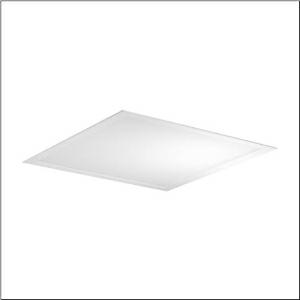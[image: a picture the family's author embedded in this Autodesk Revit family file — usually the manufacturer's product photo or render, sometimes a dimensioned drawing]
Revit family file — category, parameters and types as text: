
# Revit family: apollon_21_square_51mq11wc2454
name_source: partatom
category: Lighting Fixtures
units: mm (PartAtom-declared; Revit-internal decimal feet)

## family parameters
Cut with Voids When Loaded = No
Host = Face
Light Source = No
Part Type = Normal
Room Calculation Point = No
Round Connector Dimension = Use Diameter
Shared = No

## types (1)
- Apollon 21 square (1 x LED, 4200 lm, 24.7 W, 4000K)
    Apparent Load = 25 VA
    CIE Flux Codes = 60 87 97 100 100
    Color Rendering = 80
    Color Temperature = 4000K
    Default Elevation = 1800 mm
    Description = Apollon 21 square, office luminaire, primary optical cover: micro prismatic cover, of PMMA, CAT 2 (L<= 3000cd/m²), light emission: direct distribution, primary light characteristic: symmetric, installation type: lay-in mounting, LED, rated luminous flux: 4.200lm, luminous efficacy: 170lm/W, light colour: 840, colour temperature: 4000K, control gear: DALI 2, Multilumen, with terminal, 5-pole, mains connection: 220..240V, AC/DC, 0/50..60Hz, rated input power: 24.7W, housing, of aluminium, coated, traffic white (RAL 9016), module: M625, length: 620mm, width: 620mm, height: 55mm, recess depth: 180mm, housing upper side, of sheet steel, galvanised, protection rating (complete): IP20, protection rating (lamp compartment, on room side): IP54, insulation class (complete): insulation class II (safety insulation), certification: CE, ENEC, impact resistance: IK03, permissible operating ambient temperature: -20..+45°C, permissible storage temperature: -40..+80°C, standard: EN 60598-2-22, packaging unit: 1 piece
    Height = 0 mm  [stored 0 ft]
    Lamp = 1 x LED
    Lamp Light Flux = 4200 lm
    Lamp Power = 24.7 W
    Lamp count = 1
    Length = 620 mm
    Luminous efficacy = 170 lm/W
    Manufacturer = Siteco
    ModVariant = No
    Model = 51MQ11WC2454
    Mounting Place = Ceiling
    Mounting Type = Recessed
    Number of Poles = 1
    OnlyDefault = Yes
    Power Factor = 1
    Product Name = Apollon 21 square
    Product group = office luminaire | ceiling recessed
    ProductGroupID = 401
    Protection Class = Protection class II
    Protection Degree = IP 20
    RLX_Detail_Level = 1
    RLX_Emergency_Light_Flux = 0 lm
    RLX_Emergency_Type = 0
    RLX_Emergency_Type_DB = No
    RlxData = <blob elided: 13013 chars, md5=5b942ec0>
    Socket = socket
    Standby Power = 0 W
    System Light Flux = 4200 lm
    System Power = 25 W
    Type Comments = Product without accessories
    Type Image = l_1291054.jpg
    URL = http://relux.com
    VarID = ---
    Voltage = 0 V
    Weight = 0.00 kg
    Width = 620 mm

note: [stored X ft] marks values corroborated as IEEE doubles in the binary element streams (Revit-internal decimal feet)

## geometry (parser evidence)
native form markers: Sweep x9
no freeform markers — native parametric forms only
